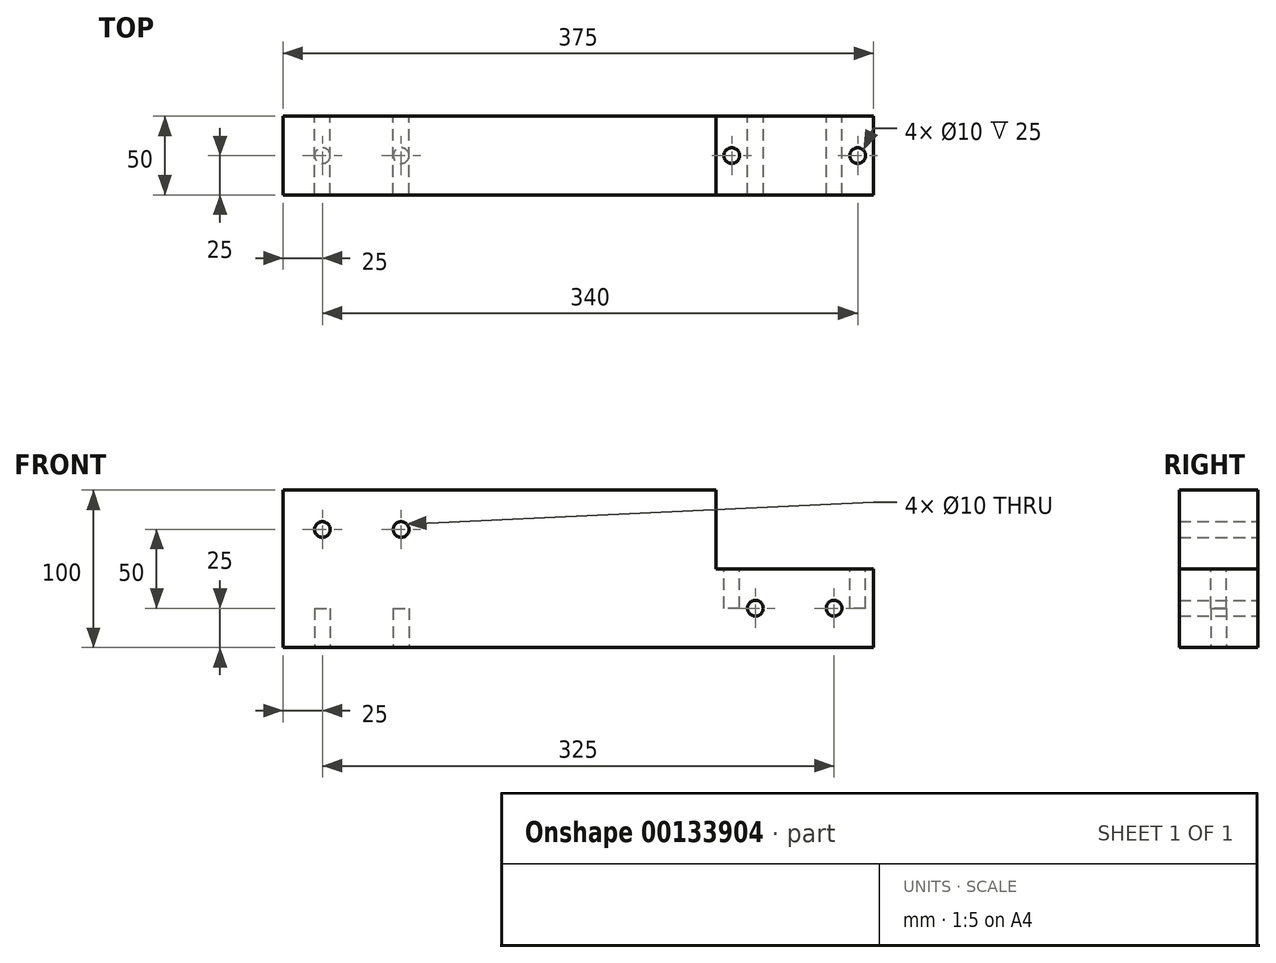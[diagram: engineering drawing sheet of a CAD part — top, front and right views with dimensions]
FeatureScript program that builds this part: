
annotation { "Feature Type Name" : "Feature", "Feature Type Description" : "" }
export const myFeature = defineFeature(function(context is Context, id is Id, definition is map)
    precondition{}
    {
        {
            var Q0;
            Q0=qCreatedBy(makeId("Front.planeOp"),FACE);
            var sketch = newSketch(context, id + "F0", { "sketchPlane" : qUnion([Q0])});
            skLineSegment(sketch, "E0.bottom", {"start": v(187.5, -50) * mm, "end": v(-187.5, -50) * mm});
            skLineSegment(sketch, "E0.top", {"start": v(187.5, 50) * mm, "end": v(-187.5, 50) * mm});
            skLineSegment(sketch, "E0.left", {"start": v(187.5, -50) * mm, "end": v(187.5, 50) * mm});
            skLineSegment(sketch, "E0.right", {"start": v(-187.5, -50) * mm, "end": v(-187.5, 50) * mm});
            skPoint(sketch, "E0.middle", {"position": v(0, 0) * mm});
            skSolve(sketch);
        }
        {
            var Q0;
            Q0=makeQuery(id+"F0.imprint","IMPRINT",FACE,{"disambiguationData":[TD([[makeQuery(id+"F0.imprint","IMPRINT",EDGE,{"derivedFrom":sQuery(id+"F0.wireOp",EDGE,"E0.bottom")}),-1.0]])]});
            extrude(context, id + "F1", {"entities" : qUnion([Q0]), "depth" : 50 * mm});
        }
        {
            var Q0;
            Q0=makeQuery(id+"F1.opExtrude","SWEPT_FACE",FACE,{"disambiguationData":[OSD([sQuery(id+"F0.wireOp",EDGE,"E0.top")])]});
            var sketch = newSketch(context, id + "F2", { "sketchPlane" : qUnion([Q0])});
            skCircle(sketch, "E1", {"center": v(97.5, -25) * mm, "radius": 5 * mm});
            skCircle(sketch, "E2", {"center": v(177.5, -25) * mm, "radius": 5 * mm});
            skSolve(sketch);
        }
        {
            var Q0;
            Q0=makeQuery(id+"F2.imprint","IMPRINT",FACE,{"disambiguationData":[TD([[makeQuery(id+"F2.imprint","IMPRINT",EDGE,{"derivedFrom":sQuery(id+"F2.wireOp",EDGE,"E1")}),1.0]])]});
            var Q1;
            Q1=makeQuery(id+"F2.imprint","IMPRINT",FACE,{"disambiguationData":[TD([[makeQuery(id+"F2.imprint","IMPRINT",EDGE,{"derivedFrom":sQuery(id+"F2.wireOp",EDGE,"E2")}),1.0]])]});
            extrude(context, id + "F3", {"entities" : qUnion([Q0, Q1]), "operationType" : NewBodyOperationType.REMOVE, "oppositeDirection" : true, "depth" : 75 * mm});
        }
        {
            var Q0;
            Q0=makeQuery(id+"F1.opExtrude","CAP_FACE",FACE,{"disambiguationData":[OSD([sQuery(id+"F0.wireOp",EDGE,"E0.bottom"),sQuery(id+"F0.wireOp",EDGE,"E0.top"),sQuery(id+"F0.wireOp",EDGE,"E0.left"),sQuery(id+"F0.wireOp",EDGE,"E0.right")])],"isStart":false});
            var sketch = newSketch(context, id + "F4", { "sketchPlane" : qUnion([Q0])});
            skPoint(sketch, "E3.oppositeSnap0", {"position": v(187.5, 0) * mm});
            skLineSegment(sketch, "E3.bottom", {"start": v(187.5, 50) * mm, "end": v(87.5, 50) * mm});
            skLineSegment(sketch, "E3.top", {"start": v(187.5, 0) * mm, "end": v(87.5, 0) * mm});
            skLineSegment(sketch, "E3.left", {"start": v(187.5, 50) * mm, "end": v(187.5, 0) * mm});
            skLineSegment(sketch, "E3.right", {"start": v(87.5, 50) * mm, "end": v(87.5, 0) * mm});
            skSolve(sketch);
        }
        {
            var Q0;
            Q0=makeQuery(id+"F4.imprint","IMPRINT",FACE,{"disambiguationData":[TD([[makeQuery(id+"F4.imprint","IMPRINT",EDGE,{"derivedFrom":sQuery(id+"F4.wireOp",EDGE,"E3.bottom")}),1.0]])]});
            extrude(context, id + "F5", {"entities" : qUnion([Q0]), "operationType" : NewBodyOperationType.REMOVE, "endBound" : BoundingType.THROUGH_ALL, "oppositeDirection" : true, "depth" : 25 * mm});
        }
        {
            var Q0;
            Q0=makeQuery(id+"F1.opExtrude","CAP_FACE",FACE,{"disambiguationData":[OSD([sQuery(id+"F0.wireOp",EDGE,"E0.bottom"),sQuery(id+"F0.wireOp",EDGE,"E0.top"),sQuery(id+"F0.wireOp",EDGE,"E0.left"),sQuery(id+"F0.wireOp",EDGE,"E0.right")])],"isStart":true});
            var sketch = newSketch(context, id + "F6", { "sketchPlane" : qUnion([Q0])});
            skCircle(sketch, "E4", {"center": v(-112.5, -25) * mm, "radius": 5 * mm});
            skCircle(sketch, "E5", {"center": v(-162.5, -25) * mm, "radius": 5 * mm});
            skCircle(sketch, "E6", {"center": v(162.5, 25) * mm, "radius": 5 * mm});
            skCircle(sketch, "E7", {"center": v(112.5, 25) * mm, "radius": 5 * mm});
            skSolve(sketch);
        }
        {
            var Q0;
            Q0=makeQuery(id+"F6.imprint","IMPRINT",FACE,{"disambiguationData":[TD([[makeQuery(id+"F6.imprint","IMPRINT",EDGE,{"derivedFrom":sQuery(id+"F6.wireOp",EDGE,"E4")}),1.0]])]});
            var Q1;
            Q1=makeQuery(id+"F6.imprint","IMPRINT",FACE,{"disambiguationData":[TD([[makeQuery(id+"F6.imprint","IMPRINT",EDGE,{"derivedFrom":sQuery(id+"F6.wireOp",EDGE,"E5")}),1.0]])]});
            var Q2;
            Q2=makeQuery(id+"F6.imprint","IMPRINT",FACE,{"disambiguationData":[TD([[makeQuery(id+"F6.imprint","IMPRINT",EDGE,{"derivedFrom":sQuery(id+"F6.wireOp",EDGE,"E6")}),1.0]])]});
            var Q3;
            Q3=makeQuery(id+"F6.imprint","IMPRINT",FACE,{"disambiguationData":[TD([[makeQuery(id+"F6.imprint","IMPRINT",EDGE,{"derivedFrom":sQuery(id+"F6.wireOp",EDGE,"E7")}),1.0]])]});
            extrude(context, id + "F7", {"entities" : qUnion([Q0, Q1, Q2, Q3]), "operationType" : NewBodyOperationType.REMOVE, "endBound" : BoundingType.THROUGH_ALL, "oppositeDirection" : true, "depth" : 25 * mm});
        }
        {
            var Q0;
            Q0=makeQuery(id+"F1.opExtrude","SWEPT_FACE",FACE,{"disambiguationData":[OSD([sQuery(id+"F0.wireOp",EDGE,"E0.bottom")])]});
            var sketch = newSketch(context, id + "F8", { "sketchPlane" : qUnion([Q0])});
            skCircle(sketch, "E8", {"center": v(-162.5, 25) * mm, "radius": 5 * mm});
            skPoint(sketch, "E8.centerSnap0", {"position": v(-187.5, 25) * mm});
            skCircle(sketch, "E9", {"center": v(-112.5, 25) * mm, "radius": 5 * mm});
            skSolve(sketch);
        }
        {
            var Q0;
            Q0=makeQuery(id+"F8.imprint","IMPRINT",FACE,{"disambiguationData":[TD([[makeQuery(id+"F8.imprint","IMPRINT",EDGE,{"derivedFrom":sQuery(id+"F8.wireOp",EDGE,"E8")}),1.0]])]});
            var Q1;
            Q1=makeQuery(id+"F8.imprint","IMPRINT",FACE,{"disambiguationData":[TD([[makeQuery(id+"F8.imprint","IMPRINT",EDGE,{"derivedFrom":sQuery(id+"F8.wireOp",EDGE,"E9")}),1.0]])]});
            extrude(context, id + "F9", {"entities" : qUnion([Q0, Q1]), "operationType" : NewBodyOperationType.REMOVE, "oppositeDirection" : true, "depth" : 25 * mm});
        }
    });
